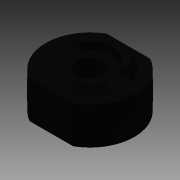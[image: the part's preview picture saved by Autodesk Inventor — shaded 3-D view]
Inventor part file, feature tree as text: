
AUTODESK INVENTOR PART (.ipt)
format: ipt  version: 2015 SP1 (Build 190203100, 203)  size: 232,448 bytes
history: native  units: in
note: dims shown in document units (in); Inventor stores cm internally (conversion verified against a paired STEP export)
features: other x2, imported_body x2, mirror x1
ambient origin geometry x8: Origin, YZ Plane, XZ Plane, XY Plane, X Axis, Y Axis, Z Axis, Center Point
bodies: Body1 (feature_tree), Body2 (feature_tree)
feature tree (5):
  mirror  "Mirror2"
  other  "228-2500-143-STEP1"
  other  "Boss-Extrude7"
  imported_body  "Base1"
  imported_body  "Base2"
